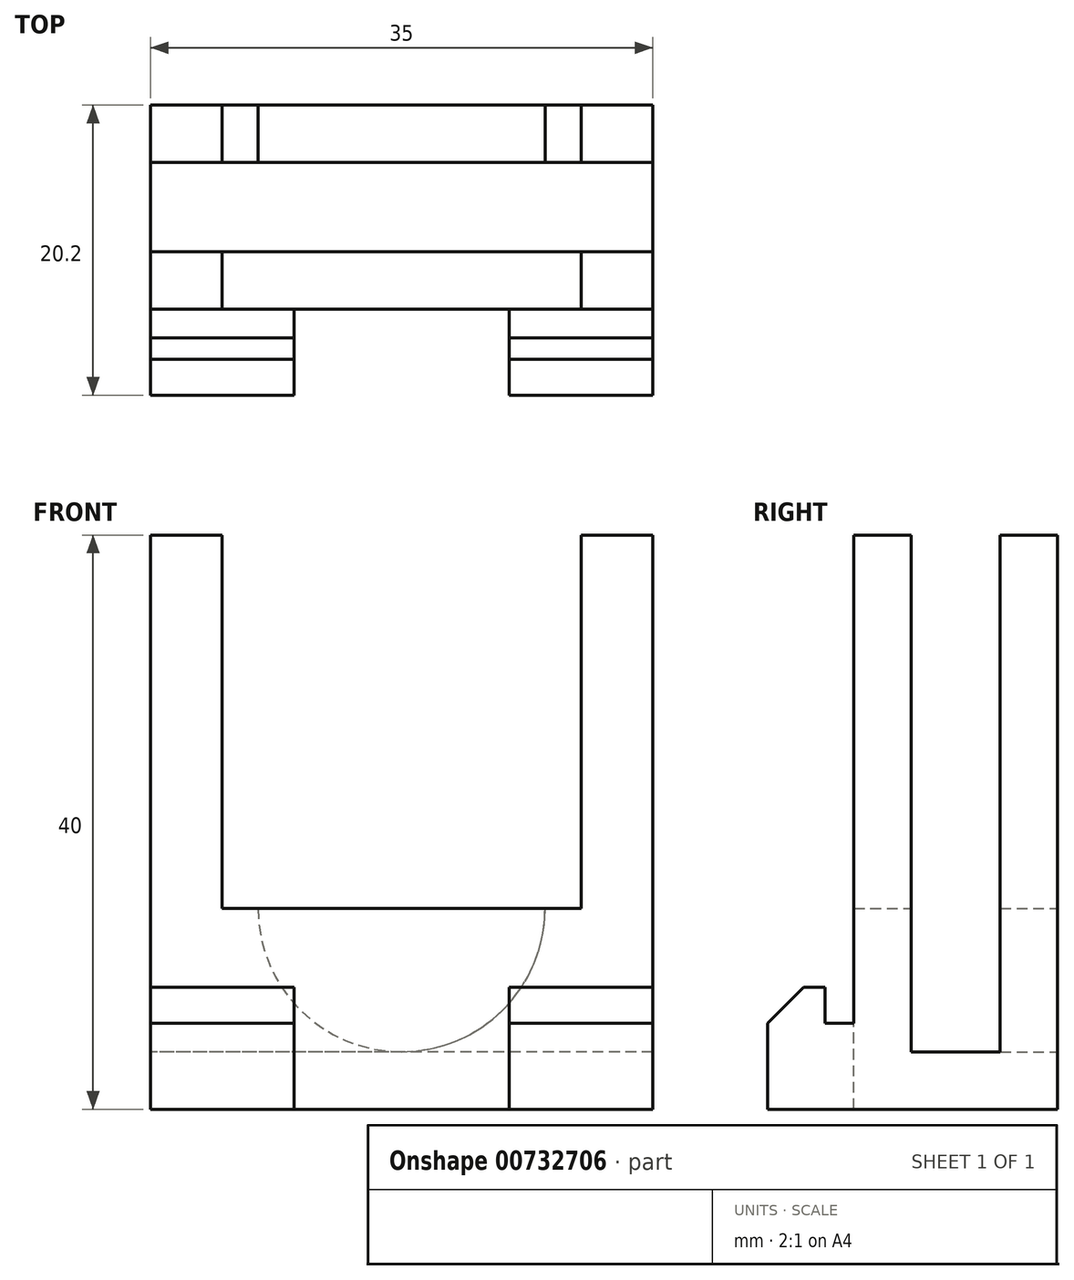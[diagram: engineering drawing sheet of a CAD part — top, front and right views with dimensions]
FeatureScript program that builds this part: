
annotation { "Feature Type Name" : "Feature", "Feature Type Description" : "" }
export const myFeature = defineFeature(function(context is Context, id is Id, definition is map)
    precondition{}
    {
        {
            var Q0;
            Q0=qCreatedBy(makeId("Right.planeOp"),FACE);
            var sketch = newSketch(context, id + "F0", { "sketchPlane" : qUnion([Q0])});
            skLineSegment(sketch, "E0", {"start": v(-2.33, 40) * mm, "end": v(-2.33, 0) * mm});
            skLineSegment(sketch, "E1", {"start": v(-2.33, 0) * mm, "end": v(11.87, 0) * mm});
            skLineSegment(sketch, "E2", {"start": v(11.87, 0) * mm, "end": v(11.87, 40) * mm});
            skLineSegment(sketch, "E3", {"start": v(1.67, 4) * mm, "end": v(1.67, 40) * mm});
            skLineSegment(sketch, "E4", {"start": v(1.67, 40) * mm, "end": v(-2.33, 40) * mm});
            skLineSegment(sketch, "E5", {"start": v(1.67, 4) * mm, "end": v(7.87, 4) * mm});
            skLineSegment(sketch, "E6", {"start": v(7.87, 4) * mm, "end": v(7.87, 40) * mm});
            skLineSegment(sketch, "E7", {"start": v(7.87, 40) * mm, "end": v(11.87, 40) * mm});
            skLineSegment(sketch, "E8", {"start": v(-2.33, 0) * mm, "end": v(-8.33, 0) * mm});
            skLineSegment(sketch, "E9", {"start": v(-8.33, 0) * mm, "end": v(-8.33, 6) * mm});
            skLineSegment(sketch, "E10", {"start": v(-8.33, 6) * mm, "end": v(-5.83, 8.5) * mm});
            skLineSegment(sketch, "E11", {"start": v(-5.83, 8.5) * mm, "end": v(-4.33, 8.5) * mm});
            skLineSegment(sketch, "E12", {"start": v(-4.33, 8.5) * mm, "end": v(-4.33, 6) * mm});
            skLineSegment(sketch, "E13", {"start": v(-4.33, 6) * mm, "end": v(-2.33, 6) * mm});
            skLineSegment(sketch, "E14", {"start": v(-4.33, 6) * mm, "end": v(-8.33, 6) * mm, "construction": true});
            skLineSegment(sketch, "E15", {"start": v(-4.33, 8.5) * mm, "end": v(-4.33, 0) * mm, "construction": true});
            skSolve(sketch);
        }
        {
            var Q0;
            Q0 = qSketchRegion(id + "F0", true);
            extrude(context, id + "F1", {"entities" : qUnion([Q0]), "depth" : 35 * mm, "offsetDistance" : 25 * mm});
        }
        {
            var Q0;
            Q0=makeQuery(id+"F1.opExtrude","SWEPT_FACE",FACE,{"disambiguationData":[OSD([sQuery(id+"F0.wireOp",EDGE,"E3")])]});
            var sketch = newSketch(context, id + "F2", { "sketchPlane" : qUnion([Q0])});
            skLineSegment(sketch, "E16.bottom", {"start": v(-30, 40) * mm, "end": v(-5, 40) * mm});
            skLineSegment(sketch, "E16.top", {"start": v(-30, 14) * mm, "end": v(-5, 14) * mm});
            skLineSegment(sketch, "E16.left", {"start": v(-30, 40) * mm, "end": v(-30, 14) * mm});
            skLineSegment(sketch, "E16.right", {"start": v(-5, 40) * mm, "end": v(-5, 14) * mm});
            skLineSegment(sketch, "E17", {"start": v(-17.5, 40) * mm, "end": v(-17.5, 4) * mm, "construction": true});
            skLineSegment(sketch, "E18", {"start": v(-35, 40) * mm, "end": v(0, 40) * mm, "construction": true});
            skSolve(sketch);
        }
        {
            var Q0;
            Q0 = qSketchRegion(id + "F2", true);
            extrude(context, id + "F3", {"entities" : qUnion([Q0]), "operationType" : NewBodyOperationType.REMOVE, "endBound" : BoundingType.THROUGH_ALL, "oppositeDirection" : true, "depth" : 25 * mm, "offsetDistance" : 25 * mm, "hasSecondDirection" : true, "secondDirectionBound" : SecondDirectionBoundingType.THROUGH_ALL, "secondDirectionOppositeDirection" : false, "secondDirectionDepth" : 25 * mm});
        }
        {
            var Q0;
            Q0=makeQuery(id+"F1.opExtrude","SWEPT_FACE",FACE,{"disambiguationData":[OSD([sQuery(id+"F0.wireOp",EDGE,"E9")])]});
            var sketch = newSketch(context, id + "F4", { "sketchPlane" : qUnion([Q0])});
            skLineSegment(sketch, "E19.bottom", {"start": v(10, 0) * mm, "end": v(25, 0) * mm});
            skLineSegment(sketch, "E19.top", {"start": v(10, 6) * mm, "end": v(25, 6) * mm});
            skLineSegment(sketch, "E19.left", {"start": v(10, 0) * mm, "end": v(10, 6) * mm});
            skLineSegment(sketch, "E19.right", {"start": v(25, 0) * mm, "end": v(25, 6) * mm});
            skPoint(sketch, "E20", {"position": v(17.5, 6) * mm});
            skLineSegment(sketch, "E21", {"start": v(10, 6) * mm, "end": v(0, 6) * mm, "construction": true});
            skLineSegment(sketch, "E22", {"start": v(25, 6) * mm, "end": v(35, 6) * mm, "construction": true});
            skLineSegment(sketch, "E23.top", {"start": v(10, 8.5) * mm, "end": v(25, 8.5) * mm});
            skLineSegment(sketch, "E23.left", {"start": v(10, 6) * mm, "end": v(10, 8.5) * mm});
            skLineSegment(sketch, "E23.right", {"start": v(25, 6) * mm, "end": v(25, 8.5) * mm});
            skSolve(sketch);
        }
        {
            var Q0;
            Q0 = qSketchRegion(id + "F4", true);
            var Q1;
            Q1=makeQuery(id+"F1.opExtrude","SWEPT_FACE",FACE,{"disambiguationData":[OSD([sQuery(id+"F0.wireOp",EDGE,"E0")])]});
            extrude(context, id + "F5", {"entities" : qUnion([Q0]), "operationType" : NewBodyOperationType.REMOVE, "endBound" : BoundingType.UP_TO_SURFACE, "oppositeDirection" : true, "depth" : 25 * mm, "endBoundEntityFace" : qUnion([Q1]), "offsetDistance" : 25 * mm});
        }
        {
            var Q0;
            Q0=makeQuery(id+"F1.opExtrude","SWEPT_FACE",FACE,{"disambiguationData":[OSD([sQuery(id+"F0.wireOp",EDGE,"E2")])]});
            var sketch = newSketch(context, id + "F6", { "sketchPlane" : qUnion([Q0])});
            skPoint(sketch, "E24", {"position": v(-17.5, 14) * mm});
            skCircle(sketch, "E25", {"center": v(-17.5, 14) * mm, "radius": 10 * mm});
            skSolve(sketch);
        }
        {
            var Q0;
            Q0 = qSketchRegion(id + "F6", true);
            extrude(context, id + "F7", {"entities" : qUnion([Q0]), "operationType" : NewBodyOperationType.REMOVE, "endBound" : BoundingType.UP_TO_NEXT, "oppositeDirection" : true, "depth" : 25 * mm, "offsetDistance" : 25 * mm});
        }
    });
